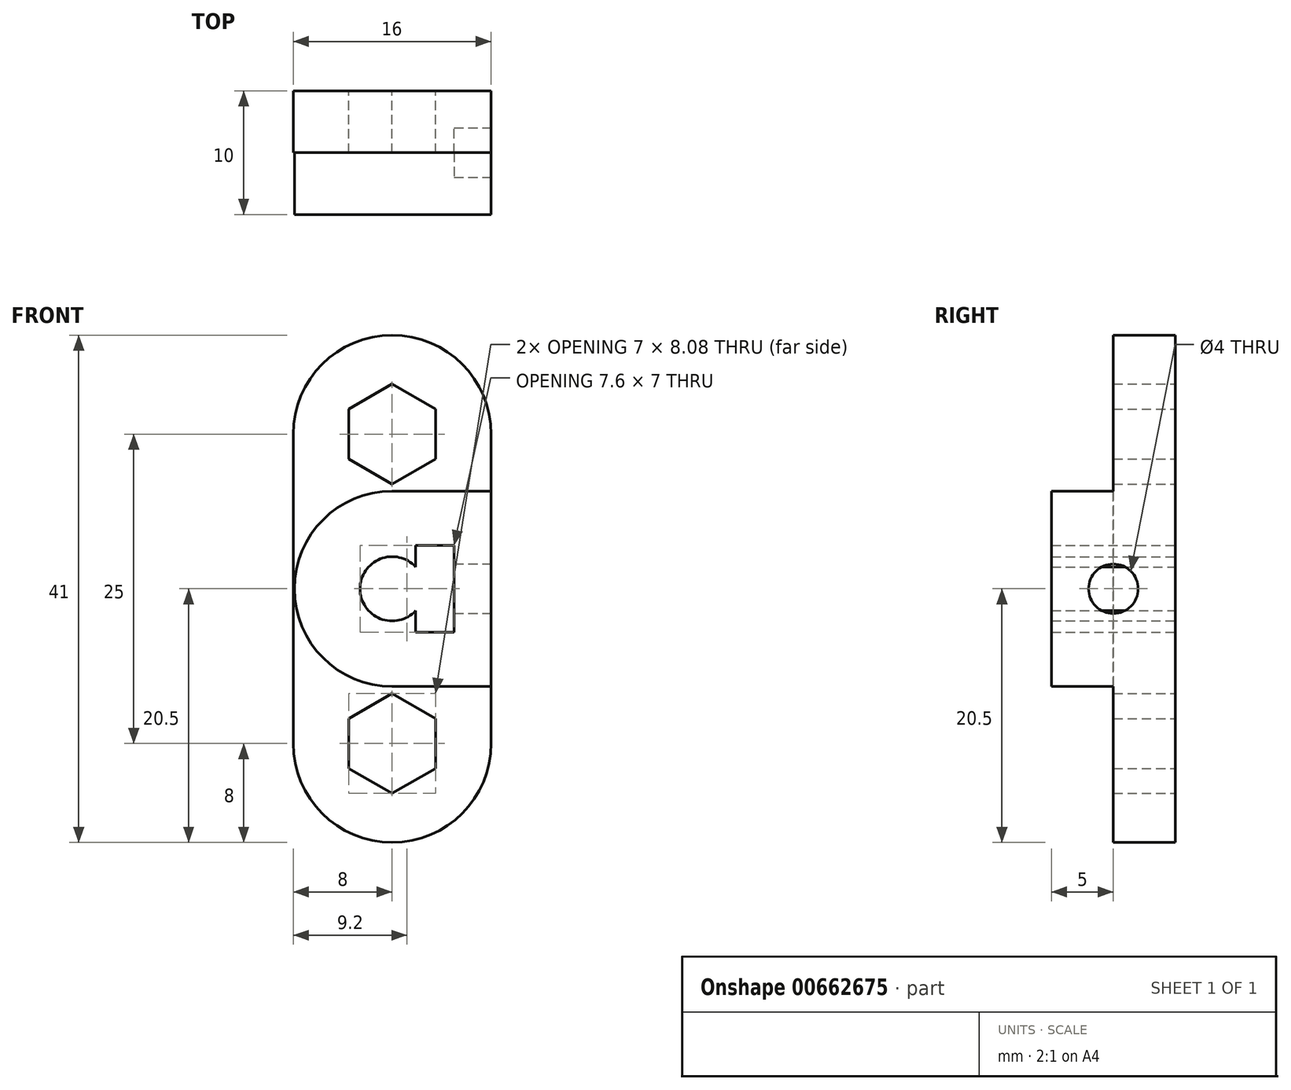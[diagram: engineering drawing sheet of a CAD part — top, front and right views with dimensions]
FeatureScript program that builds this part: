
annotation { "Feature Type Name" : "Feature", "Feature Type Description" : "" }
export const myFeature = defineFeature(function(context is Context, id is Id, definition is map)
    precondition{}
    {
        {
            var Q0;
            Q0=qCreatedBy(makeId("Front.planeOp"),FACE);
            var sketch = newSketch(context, id + "F0", { "sketchPlane" : qUnion([Q0])});
            skLineSegment(sketch, "E0.bottom", {"start": v(8, -12.5) * mm, "end": v(-8, -12.5) * mm, "construction": true});
            skLineSegment(sketch, "E0.top", {"start": v(8, 12.5) * mm, "end": v(-8, 12.5) * mm, "construction": true});
            skLineSegment(sketch, "E0.left", {"start": v(8, -12.5) * mm, "end": v(8, 12.5) * mm});
            skLineSegment(sketch, "E0.right", {"start": v(-8, -12.5) * mm, "end": v(-8, 12.5) * mm});
            skPoint(sketch, "E0.middle", {"position": v(0, 0) * mm});
            skArc(sketch, "E1", {"start": v(8, 12.5) * mm, "mid": v(0, 20.5) * mm, "end": v(-8, 12.5) * mm});
            skArc(sketch, "E2", {"start": v(-8, -12.5) * mm, "mid": v(0, -20.5) * mm, "end": v(8, -12.5) * mm});
            skCircle(sketch, "E3.cCircle", {"center": v(0, 12.5) * mm, "radius": 3.5 * mm, "construction": true});
            skLineSegment(sketch, "E3.0", {"start": v(3.5, 14.52) * mm, "end": v(3.5, 10.48) * mm});
            skLineSegment(sketch, "E3.1", {"start": v(3.5, 10.48) * mm, "end": v(0, 8.46) * mm});
            skLineSegment(sketch, "E3.2", {"start": v(0, 8.46) * mm, "end": v(-3.5, 10.48) * mm});
            skLineSegment(sketch, "E3.3", {"start": v(-3.5, 10.48) * mm, "end": v(-3.5, 14.52) * mm});
            skLineSegment(sketch, "E3.4", {"start": v(-3.5, 14.52) * mm, "end": v(0, 16.54) * mm});
            skLineSegment(sketch, "E3.5", {"start": v(0, 16.54) * mm, "end": v(3.5, 14.52) * mm});
            skPoint(sketch, "E3.0.midPoint", {"position": v(3.5, 12.5) * mm});
            skCircle(sketch, "E4.cCircle", {"center": v(0, -12.5) * mm, "radius": 3.5 * mm, "construction": true});
            skLineSegment(sketch, "E4.0", {"start": v(3.5, -10.48) * mm, "end": v(3.5, -14.52) * mm});
            skLineSegment(sketch, "E4.1", {"start": v(3.5, -14.52) * mm, "end": v(0, -16.54) * mm});
            skLineSegment(sketch, "E4.2", {"start": v(0, -16.54) * mm, "end": v(-3.5, -14.52) * mm});
            skLineSegment(sketch, "E4.3", {"start": v(-3.5, -14.52) * mm, "end": v(-3.5, -10.48) * mm});
            skLineSegment(sketch, "E4.4", {"start": v(-3.5, -10.48) * mm, "end": v(0, -8.46) * mm});
            skLineSegment(sketch, "E4.5", {"start": v(0, -8.46) * mm, "end": v(3.5, -10.48) * mm});
            skPoint(sketch, "E4.0.midPoint", {"position": v(3.5, -12.5) * mm});
            skArc(sketch, "E5", {"start": v(1.9, 1.77) * mm, "mid": v(-2.6, 0) * mm, "end": v(1.9, -1.77) * mm});
            skLineSegment(sketch, "E6.bottom", {"start": v(5, -3.5) * mm, "end": v(1.9, -3.5) * mm});
            skLineSegment(sketch, "E6.top", {"start": v(5, 3.5) * mm, "end": v(1.9, 3.5) * mm});
            skLineSegment(sketch, "E6.left", {"start": v(5, -3.5) * mm, "end": v(5, 3.5) * mm});
            skLineSegment(sketch, "E6.right", {"start": v(1.9, -3.5) * mm, "end": v(1.9, -1.77) * mm});
            skPoint(sketch, "E6.middle", {"position": v(3.45, 0) * mm});
            skLineSegment(sketch, "E7", {"start": v(3.45, 0) * mm, "end": v(-2.6, 0) * mm, "construction": true});
            skLineSegment(sketch, "E8.trimOffspring", {"start": v(1.9, 1.77) * mm, "end": v(1.9, 3.5) * mm});
            skSolve(sketch);
        }
        {
            var Q0;
            Q0=qSketchRegion(id+"F0",true);
            extrude(context, id + "F1", {"entities" : qUnion([Q0]), "depth" : 5 * mm});
        }
        {
            var Q0;
            Q0=makeQuery(id+"F1.opExtrude","CAP_FACE",FACE,{"disambiguationData":[OSD([sQuery(id+"F0.wireOp",EDGE,"E0.left"),sQuery(id+"F0.wireOp",EDGE,"E0.right"),sQuery(id+"F0.wireOp",EDGE,"E1"),sQuery(id+"F0.wireOp",EDGE,"E2"),sQuery(id+"F0.wireOp",EDGE,"E3.0"),sQuery(id+"F0.wireOp",EDGE,"E3.1"),sQuery(id+"F0.wireOp",EDGE,"E3.2"),sQuery(id+"F0.wireOp",EDGE,"E3.3"),sQuery(id+"F0.wireOp",EDGE,"E3.4"),sQuery(id+"F0.wireOp",EDGE,"E3.5"),sQuery(id+"F0.wireOp",EDGE,"E4.0"),sQuery(id+"F0.wireOp",EDGE,"E4.1"),sQuery(id+"F0.wireOp",EDGE,"E4.2"),sQuery(id+"F0.wireOp",EDGE,"E4.3"),sQuery(id+"F0.wireOp",EDGE,"E4.4"),sQuery(id+"F0.wireOp",EDGE,"E4.5"),sQuery(id+"F0.wireOp",EDGE,"E5"),sQuery(id+"F0.wireOp",EDGE,"E6.bottom"),sQuery(id+"F0.wireOp",EDGE,"E6.top"),sQuery(id+"F0.wireOp",EDGE,"E6.left"),sQuery(id+"F0.wireOp",EDGE,"E6.right"),sQuery(id+"F0.wireOp",EDGE,"E8.trimOffspring")])],"isStart":false});
            var sketch = newSketch(context, id + "F2", { "sketchPlane" : qUnion([Q0])});
            skLineSegment(sketch, "E9", {"start": v(0, -8.46) * mm, "end": v(0, 8.46) * mm, "construction": true});
            skLineSegment(sketch, "E10", {"start": v(0, 8.46) * mm, "end": v(-8, 0) * mm, "construction": true});
            skLineSegment(sketch, "E11", {"start": v(-8, 0) * mm, "end": v(0, 0) * mm, "construction": true});
            skArc(sketch, "E12", {"start": v(0, 7.9) * mm, "mid": v(-7.9, 0) * mm, "end": v(0, -7.9) * mm});
            skLineSegment(sketch, "E13", {"start": v(8, -7.9) * mm, "end": v(0, -7.9) * mm});
            skLineSegment(sketch, "E14", {"start": v(8, 7.9) * mm, "end": v(0, 7.9) * mm});
            skArc(sketch, "E15.0", {"start": v(1.9, 1.77) * mm, "mid": v(-2.6, 0) * mm, "end": v(1.9, -1.77) * mm});
            skLineSegment(sketch, "E16.0", {"start": v(1.9, 1.77) * mm, "end": v(1.9, 3.5) * mm});
            skLineSegment(sketch, "E17.0", {"start": v(5, -3.5) * mm, "end": v(5, 3.5) * mm});
            skLineSegment(sketch, "E18.0", {"start": v(1.9, -3.5) * mm, "end": v(1.9, -1.77) * mm});
            skLineSegment(sketch, "E19.0", {"start": v(5, -3.5) * mm, "end": v(1.9, -3.5) * mm});
            skLineSegment(sketch, "E20.0", {"start": v(5, 3.5) * mm, "end": v(1.9, 3.5) * mm});
            skSolve(sketch);
        }
        {
            var Q0;
            Q0=makeQuery(id+"F2.imprint","IMPRINT",FACE,{"disambiguationData":[TD([[makeQuery(id+"F2.imprint","IMPRINT",EDGE,{"derivedFrom":sQuery(id+"F2.wireOp",EDGE,"E12")}),1.0]])]});
            extrude(context, id + "F3", {"entities" : qUnion([Q0]), "operationType" : NewBodyOperationType.ADD, "depth" : 5 * mm});
        }
        {
            var Q0;
            {var subQ0=sQuery(id+"F0.wireOp",EDGE,"E0.left");Q0=makeQuery(id+"F3.boolean.opBoolean","MERGE",FACE,{"derivedFrom":[makeQuery(id+"F1.opExtrude","SWEPT_FACE",FACE,{"disambiguationData":[OSD([subQ0])]}),makeQuery(id+"F3.opExtrude","SWEPT_FACE",FACE,{"disambiguationData":[OSD([subQ0])]})]});}
            var sketch = newSketch(context, id + "F4", { "sketchPlane" : qUnion([Q0])});
            skLineSegment(sketch, "E21", {"start": v(-10, 0) * mm, "end": v(0, 0) * mm, "construction": true});
            skLineSegment(sketch, "E22", {"start": v(-5, -7.9) * mm, "end": v(-5, 7.9) * mm, "construction": true});
            skCircle(sketch, "E23", {"center": v(-5, 0) * mm, "radius": 2 * mm});
            skSolve(sketch);
        }
        {
            var Q0;
            Q0=makeQuery(id+"F4.imprint","IMPRINT",FACE,{"disambiguationData":[TD([[makeQuery(id+"F4.imprint","IMPRINT",EDGE,{"derivedFrom":sQuery(id+"F4.wireOp",EDGE,"E23")}),1.0]])]});
            var Q1;
            Q1=makeQuery(id+"F3.boolean.opBoolean","MERGE",FACE,{"derivedFrom":[makeQuery(id+"F1.opExtrude","SWEPT_FACE",FACE,{"disambiguationData":[OSD([sQuery(id+"F0.wireOp",EDGE,"E6.right")])]}),makeQuery(id+"F3.opExtrude","SWEPT_FACE",FACE,{"disambiguationData":[OSD([sQuery(id+"F2.wireOp",EDGE,"E18.0")])]})]});
            extrude(context, id + "F5", {"entities" : qUnion([Q0]), "operationType" : NewBodyOperationType.REMOVE, "endBound" : BoundingType.UP_TO_SURFACE, "oppositeDirection" : true, "endBoundEntityFace" : qUnion([Q1]), "depth" : 25 * mm});
        }
    });
